# Revit family: Gira_264003
name_source: partatom
category: Elektroinstallationen
revit_build: Autodesk Revit 2017 (Build: 20160225_1515(x64)
units: mm (PartAtom-declared; Revit-internal decimal feet)

## family parameters
Basisbauteil = Fläche
Beim Laden mit Abzugskörper schneiden = Nein
Bemaßung runder Anschluss = Durchmesser verwenden
Beschriftungsausrichtung beibehalten = Nein
Gemeinsam genutzt = Nein
Raumberechnungspunkt = Nein
Teiletyp = Normal

## types (1)
- Gira_264003
    Andere Bussysteme = ohne
    Anzahl der Kanäle = 3
    Ausführung = Wandsender komplett
    Ausführung der Oberfläche = nicht zutreffend
    BIM = https://media.stage.bim.site und Tasten.rfa
    Bauelement = Sys55_Abdeckung_Schalten und Tasten
    Befestigungsart = sonstige
    Beschreibung = Abdeckung mit 30 Schrägauslass und Beschriftungsfeld für Tragring Modular Jack 2fach  Reinweiß glänzend
    Beschriftungsfeld = mit Beschriftungsfeld
    Bussystem Funkbus = Nein
    Bussystem KNX = Ja
    Bussystem KNX-Funk = Nein
    Bussystem LON = Nein
    Bussystem Powernet = Nein
    Datenblatt = https://katalog.gira.de
    Farbe = weiß
    GTIN = 4010337460138
    Geeignet für Schutzart (IP) = IP20
    HAN = 264003
    Halogenfrei = Ja
    Hersteller = Gira
    Lüsterklemme = Nein
    Mit Aufdruck = Nein
    Mit Busankopplung = Nein
    Mit Klappdeckel = Nein
    Mit Staubschutz = Nein
    Mit Zugentlastung = Nein
    Montageart = sonstige
    Oberfläche = sonstige
    Produktseite = http://katalog.gira.de
    RAL-Nummer (ähnlich) = 9010
    Tragring = Nein
    Transparent = Nein
    Typname = Abd. 30° + BSF f. Tragring MJ 2f System 55 Reinweiß
    URL = https://www.gira.de
    Verwendung = Modular-Jack
    Vorgabe-Ansicht = 1219 mm
    Werkstoff = sonstige
    Werkstoffgüte = sonstige
    Zusammenstellung = Zentralplatte

## geometry (parser evidence)
native form markers: Sweep x8
no freeform markers — native parametric forms only
